FCSTD DOCUMENT  (FreeCAD 0.20R29603 (Git))
Label: MainSketch
License: All rights reserved
LicenseURL: http://en.wikipedia.org/wiki/All_rights_reserved
objects: Sketcher::SketchObject×3, PartDesign::Body×1
note: 4 computed .brp shape members not serialized (recipe doc carries the construction recipe); baked Part::Feature solids carry a one-line shape summary decoded from their .brp

FEATURE [Sketcher::SketchObject] Sketch003  label="body_mount_holes"
  FullyConstrained = false
  MapMode = 5
  sketch-geometry (4):
    g0: Circle CenterX=-5.5 CenterY=41.5 CenterZ=0 NormalX=0 NormalY=0 NormalZ=1 AngleXU=0 Radius=3.25
    g1: Circle CenterX=5.5 CenterY=41.5 CenterZ=0 NormalX=0 NormalY=0 NormalZ=1 AngleXU=0 Radius=3.25
    g2: Circle CenterX=-29.4289 CenterY=-36.5 CenterZ=0 NormalX=0 NormalY=0 NormalZ=1 AngleXU=0 Radius=3.25
    g3: Circle CenterX=29.4289 CenterY=-36.5 CenterZ=0 NormalX=0 NormalY=0 NormalZ=1 AngleXU=0 Radius=3.25
  constraints (7):
    c: Symmetric(g0,g1,g-2)
    c: Symmetric(g2,g3,g-2)
    c: Equal(g0,g1)
    c: Equal(g0,g2)
    c: Equal(g0,g3)
    c: Diameter(g0) = 6.5
    c: Distance(g0,g-2) = 5.5
FEATURE [Sketcher::SketchObject] Sketch001  label="pcb_outline"
  FullyConstrained = true
  MapMode = 5
  sketch-geometry (4):
    g0: LineSegment StartX=-40.5 StartY=46.5 StartZ=0 EndX=40.5 EndY=46.5 EndZ=0
    g1: LineSegment StartX=40.5 StartY=46.5 StartZ=0 EndX=40.5 EndY=-46.5 EndZ=0
    g2: LineSegment StartX=40.5 StartY=-46.5 StartZ=0 EndX=-40.5 EndY=-46.5 EndZ=0
    g3: LineSegment StartX=-40.5 StartY=-46.5 StartZ=0 EndX=-40.5 EndY=46.5 EndZ=0
  constraints (10):
    c: Coincident(g0,g1)
    c: Coincident(g1,g2)
    c: Coincident(g2,g3)
    c: Coincident(g3,g0)
    c: Horizontal(g0)
    c: Vertical(g1)
    c: Symmetric(g2,g1,g-2)
    c: Symmetric(g0,g2,g-1)
    c: DistanceX(g0,g0) = 81
    c: DistanceY(g1,g1) = 93
FEATURE [Sketcher::SketchObject] Sketch002  label="motor_mount_holes"
  FullyConstrained = true
  MapMode = 5
  sketch-geometry (8):
    g0: Circle CenterX=-35.75 CenterY=41.8 CenterZ=0 NormalX=0 NormalY=0 NormalZ=1 AngleXU=0 Radius=1.15
    g1: Circle CenterX=-35.75 CenterY=23.8 CenterZ=0 NormalX=0 NormalY=0 NormalZ=1 AngleXU=0 Radius=1.15
    g2: Circle CenterX=35.75 CenterY=41.8 CenterZ=0 NormalX=0 NormalY=0 NormalZ=1 AngleXU=0 Radius=1.15
    g3: Circle CenterX=35.75 CenterY=23.8 CenterZ=0 NormalX=0 NormalY=0 NormalZ=1 AngleXU=0 Radius=1.15
    g4: Circle CenterX=-35.75 CenterY=-10.8 CenterZ=0 NormalX=0 NormalY=0 NormalZ=1 AngleXU=0 Radius=1.15
    g5: Circle CenterX=-35.75 CenterY=-28.8 CenterZ=0 NormalX=0 NormalY=0 NormalZ=1 AngleXU=0 Radius=1.15
    g6: Circle CenterX=35.75 CenterY=-28.8 CenterZ=0 NormalX=0 NormalY=0 NormalZ=1 AngleXU=0 Radius=1.15
    g7: Circle CenterX=35.75 CenterY=-10.8 CenterZ=0 NormalX=0 NormalY=0 NormalZ=1 AngleXU=0 Radius=1.15
  constraints (8):
    c: Block(g0)
    c: Block(g2)
    c: Block(g1)
    c: Block(g3)
    c: Block(g4)
    c: Block(g5)
    c: Block(g6)
    c: Block(g7)
FEATURE [PartDesign::Body] Body
  Group = -> [Sketch003,Sketch001,Sketch002]
  Origin = -> Origin
